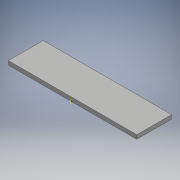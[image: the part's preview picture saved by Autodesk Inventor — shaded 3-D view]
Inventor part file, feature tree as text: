
AUTODESK INVENTOR PART (.ipt)
format: ipt  version: 2018 (Build 220112000, 112)  size: 117,760 bytes
history: native  units: mm
features: other x5, plane x1, sheet_metal_op x1, sketch x1, reference x1
ambient origin geometry x8: Origin, YZ Plane, XZ Plane, XY Plane, X Axis, Y Axis, Z Axis, Center Point
bodies: Solid1 (feature_tree)
feature tree (9):
  plane  "Work Plane1"
  sheet_metal_op  "Face1"
  other  "midtplan"
  sketch  "Sketch1"  dims[d7=3.0mm d8=12.0mm d9=12.0mm d10=26.0mm]
  reference  "Reference1"
  other  "Plate1"
  parser-record x1  (decoder bookkeeping rows leaked as tree rows — omitted from the tree; the rows remain in map.json)
  other  "modul.iam"
  other  "plade:1"
note: 1 file-system path scrubbed to <path> (originals preserved in map.json)
